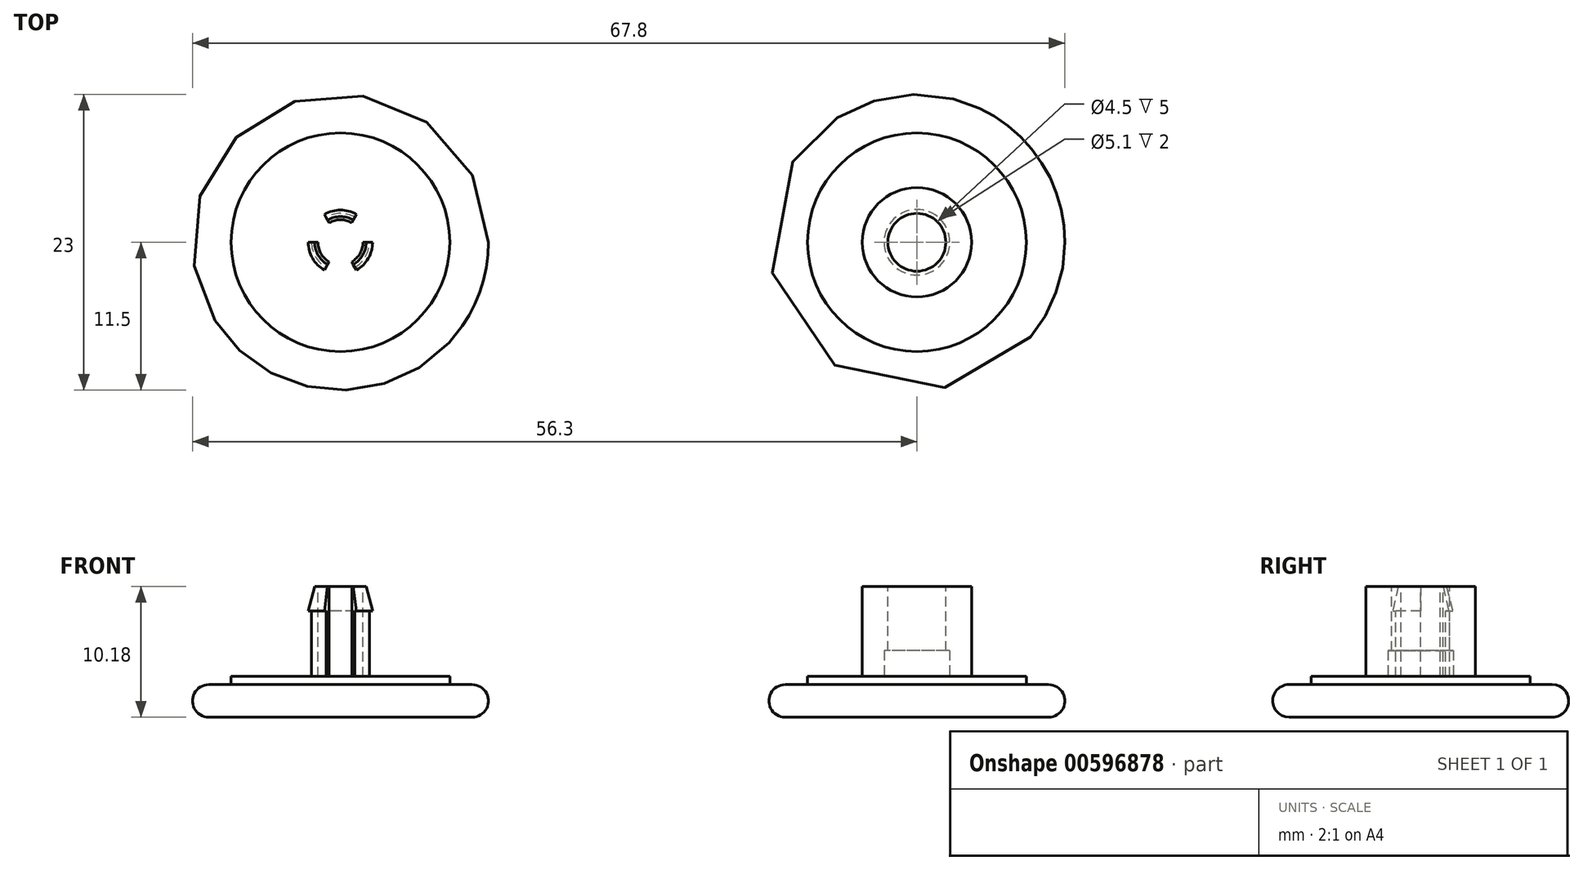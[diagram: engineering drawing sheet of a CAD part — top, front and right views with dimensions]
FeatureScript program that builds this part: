
annotation { "Feature Type Name" : "Feature", "Feature Type Description" : "" }
export const myFeature = defineFeature(function(context is Context, id is Id, definition is map)
    precondition{}
    {
        {
            var Q0;
            Q0=qCreatedBy(makeId("Top.planeOp"),FACE);
            var sketch = newSketch(context, id + "F0", { "sketchPlane" : qUnion([Q0])});
            skCircle(sketch, "E0", {"center": v(0, 0) * mm, "radius": 11.5 * mm});
            skCircle(sketch, "E1", {"center": v(0, 0) * mm, "radius": 4.25 * mm});
            skCircle(sketch, "E2", {"center": v(0, 0) * mm, "radius": 8.5 * mm});
            skSolve(sketch);
        }
        {
            var Q0;
            Q0=makeQuery(id+"F0.imprint","IMPRINT",FACE,{"disambiguationData":[TD([[makeQuery(id+"F0.imprint","IMPRINT",EDGE,{"derivedFrom":sQuery(id+"F0.wireOp",EDGE,"E0")}),1.0]])]});
            extrude(context, id + "F1", {"entities" : qUnion([Q0]), "depth" : 2.54 * mm});
        }
        {
            var Q0;
            Q0=makeQuery(id+"F0.imprint","IMPRINT",FACE,{"disambiguationData":[TD([[makeQuery(id+"F0.imprint","IMPRINT",EDGE,{"derivedFrom":sQuery(id+"F0.wireOp",EDGE,"E1")}),-1.0]])]});
            extrude(context, id + "F2", {"entities" : qUnion([Q0]), "operationType" : NewBodyOperationType.ADD, "depth" : 3.17 * mm});
        }
        {
            var Q0;
            Q0=makeQuery(id+"F0.imprint","IMPRINT",FACE,{"disambiguationData":[TD([[makeQuery(id+"F0.imprint","IMPRINT",EDGE,{"derivedFrom":sQuery(id+"F0.wireOp",EDGE,"E1")}),1.0]])]});
            extrude(context, id + "F3", {"entities" : qUnion([Q0]), "operationType" : NewBodyOperationType.ADD, "depth" : 7 * mm + 3.17 * mm});
        }
        {
            var Q0;
            Q0=makeQuery(id+"F1.opExtrude","CAP_EDGE",EDGE,{"disambiguationData":[OSD([sQuery(id+"F0.wireOp",EDGE,"E0")])],"isStart":false});
            var Q1;
            Q1=makeQuery(id+"F1.opExtrude","CAP_EDGE",EDGE,{"disambiguationData":[OSD([sQuery(id+"F0.wireOp",EDGE,"E0")])],"isStart":true});
            fillet(context, id + "F4", {"entities" : qUnion([Q0, Q1]), "radius" : 1.27 * mm, "tangentPropagation" : true, "allowEdgeOverflow" : false});
        }
        {
            var Q0;
            Q0=qCreatedBy(makeId("Top.planeOp"),FACE);
            var sketch = newSketch(context, id + "F5", { "sketchPlane" : qUnion([Q0])});
            skCircle(sketch, "E3", {"center": v(-44.8, 0) * mm, "radius": 11.5 * mm});
            skCircle(sketch, "E4", {"center": v(-44.8, 0) * mm, "radius": 8.5 * mm});
            skCircle(sketch, "E5", {"center": v(-44.8, 0) * mm, "radius": 2.5 * mm});
            skSolve(sketch);
        }
        {
            var Q0;
            Q0=makeQuery(id+"F5.imprint","IMPRINT",FACE,{"disambiguationData":[TD([[makeQuery(id+"F5.imprint","IMPRINT",EDGE,{"derivedFrom":sQuery(id+"F5.wireOp",EDGE,"E3")}),1.0]])]});
            extrude(context, id + "F6", {"entities" : qUnion([Q0]), "depth" : 2.54 * mm});
        }
        {
            var Q0;
            Q0=makeQuery(id+"F5.imprint","IMPRINT",FACE,{"disambiguationData":[TD([[makeQuery(id+"F5.imprint","IMPRINT",EDGE,{"derivedFrom":sQuery(id+"F5.wireOp",EDGE,"E4")}),1.0]])]});
            extrude(context, id + "F7", {"entities" : qUnion([Q0]), "operationType" : NewBodyOperationType.ADD, "depth" : 3.17 * mm});
        }
        {
            var Q0;
            Q0=makeQuery(id+"F5.imprint","IMPRINT",FACE,{"disambiguationData":[TD([[makeQuery(id+"F5.imprint","IMPRINT",EDGE,{"derivedFrom":sQuery(id+"F5.wireOp",EDGE,"E5")}),1.0]])]});
            extrude(context, id + "F8", {"entities" : qUnion([Q0]), "operationType" : NewBodyOperationType.ADD, "depth" : 7 * mm + 3.17 * mm});
        }
        {
            var Q0;
            Q0=makeQuery(id+"F3.opExtrude","CAP_FACE",FACE,{"disambiguationData":[OSD([sQuery(id+"F0.wireOp",EDGE,"E1")])],"isStart":false});
            var sketch = newSketch(context, id + "F9", { "sketchPlane" : qUnion([Q0])});
            skCircle(sketch, "E6", {"center": v(0, 0) * mm, "radius": 2.25 * mm});
            skSolve(sketch);
        }
        {
            var Q0;
            Q0=makeQuery(id+"F9.imprint","IMPRINT",FACE,{"disambiguationData":[TD([[makeQuery(id+"F9.imprint","IMPRINT",EDGE,{"derivedFrom":sQuery(id+"F9.wireOp",EDGE,"E6")}),1.0]])]});
            extrude(context, id + "F10", {"entities" : qUnion([Q0]), "operationType" : NewBodyOperationType.REMOVE, "oppositeDirection" : true, "depth" : 7 * mm});
        }
        {
            var Q0;
            Q0=makeQuery(id+"F6.opExtrude","CAP_EDGE",EDGE,{"disambiguationData":[OSD([sQuery(id+"F5.wireOp",EDGE,"E3")])],"isStart":false});
            var Q1;
            Q1=makeQuery(id+"F6.opExtrude","CAP_EDGE",EDGE,{"disambiguationData":[OSD([sQuery(id+"F5.wireOp",EDGE,"E3")])],"isStart":true});
            fillet(context, id + "F11", {"entities" : qUnion([Q0, Q1]), "radius" : 1.27 * mm, "tangentPropagation" : true, "allowEdgeOverflow" : false});
        }
        {
            var Q0;
            Q0=makeQuery(id+"F2.opExtrude","CAP_FACE",FACE,{"disambiguationData":[OSD([sQuery(id+"F0.wireOp",EDGE,"E1"),sQuery(id+"F0.wireOp",EDGE,"E2")])],"isStart":false});
            var sketch = newSketch(context, id + "F12", { "sketchPlane" : qUnion([Q0])});
            skCircle(sketch, "E7", {"center": v(0, 0) * mm, "radius": 2.55 * mm});
            skSolve(sketch);
        }
        {
            var Q0;
            Q0 = qSketchRegion(id + "F12", true);
            extrude(context, id + "F13", {"entities" : qUnion([Q0]), "operationType" : NewBodyOperationType.REMOVE, "depth" : 2 * mm, "offsetDistance" : 25.4 * mm});
        }
        {
            var Q0;
            Q0=qCreatedBy(makeId("Front.planeOp"),FACE);
            var sketch = newSketch(context, id + "F14", { "sketchPlane" : qUnion([Q0])});
            skLineSegment(sketch, "E8", {"start": v(-44.8, 0) * mm, "end": v(-44.8, 10.18) * mm});
            skLineSegment(sketch, "E9", {"start": v(-44.8, 10.18) * mm, "end": v(-42.55, 10.18) * mm});
            skLineSegment(sketch, "E10", {"start": v(-42.55, 8.27) * mm, "end": v(-42.3, 8.27) * mm});
            skLineSegment(sketch, "E11", {"start": v(-42.55, 8.27) * mm, "end": v(-42.55, 3.17) * mm});
            skLineSegment(sketch, "E12", {"start": v(-42.55, 10.18) * mm, "end": v(-41.88, 10.26) * mm});
            skLineSegment(sketch, "E13", {"start": v(-42.55, 3.17) * mm, "end": v(-41.9, 3.17) * mm});
            skLineSegment(sketch, "E14", {"start": v(-42.3, 8.27) * mm, "end": v(-41.64, 8.27) * mm});
            skLineSegment(sketch, "E15", {"start": v(-41.64, 8.27) * mm, "end": v(-41.88, 10.26) * mm});
            skLineSegment(sketch, "E16", {"start": v(-41.9, 3.17) * mm, "end": v(-41.64, 8.27) * mm});
            skPoint(sketch, "E17", {"position": v(-42.8, 10.18) * mm});
            skLineSegment(sketch, "E18", {"start": v(-42.3, 8.27) * mm, "end": v(-42.8, 10.18) * mm});
            skLineSegment(sketch, "E19", {"start": v(-42.55, 3.17) * mm, "end": v(-44.8, 3.17) * mm});
            skLineSegment(sketch, "E20", {"start": v(-42.8, 10.18) * mm, "end": v(-42.8, 3.17) * mm});
            skLineSegment(sketch, "E21", {"start": v(-43.3, 10.18) * mm, "end": v(-43.3, 3.17) * mm});
            skSolve(sketch);
        }
        {
            var Q0;
            Q0=makeQuery(id+"F14.imprint","IMPRINT",FACE,{"disambiguationData":[TD([[makeQuery(id+"F14.imprint","IMPRINT",EDGE,{"derivedFrom":sQuery(id+"F14.wireOp",EDGE,"E10")}),-1.0]])]});
            var Q1;
            {var subQ0=sQuery(id+"F14.wireOp",EDGE,"E12");Q1=makeQuery(id+"F14.imprint","IMPRINT",FACE,{"disambiguationData":[TD([[makeQuery(id+"F14.imprint","IMPRINT",EDGE,{"derivedFrom":subQ0}),-1.0]])]});}
            var Q2;
            Q2=sQuery(id+"F14.wireOp",EDGE,"E8");
            revolve(context, id + "F15", {"operationType" : NewBodyOperationType.REMOVE, "entities" : qUnion([Q0, Q1]), "axis" : qUnion([Q2]), "revolveType" : RevolveType.FULL, "oppositeDirection" : true});
        }
        {
            var Q0;
            Q0=makeQuery(id+"F8.opExtrude","CAP_FACE",FACE,{"disambiguationData":[OSD([sQuery(id+"F5.wireOp",EDGE,"E5")])],"isStart":false});
            var sketch = newSketch(context, id + "F16", { "sketchPlane" : qUnion([Q0])});
            skCircle(sketch, "E22", {"center": v(-44.8, 0) * mm, "radius": 1.75 * mm});
            skSolve(sketch);
        }
        {
            var Q0;
            Q0 = qSketchRegion(id + "F16", true);
            extrude(context, id + "F17", {"entities" : qUnion([Q0]), "operationType" : NewBodyOperationType.REMOVE, "oppositeDirection" : true, "depth" : 7 * mm, "offsetDistance" : 25.4 * mm});
        }
        {
            var Q0;
            Q0=makeQuery(id+"F15.boolean.opBoolean","MERGE",FACE,{"derivedFrom":[makeQuery(id+"F7.opExtrude","CAP_FACE",FACE,{"disambiguationData":[OSD([sQuery(id+"F5.wireOp",EDGE,"E4"),sQuery(id+"F5.wireOp",EDGE,"E5")])],"isStart":false}),makeQuery(id+"F15.opRevolve","SWEPT_FACE",FACE,{"disambiguationData":[OSD([sQuery(id+"F14.wireOp",EDGE,"E13")])]})]});
            var sketch = newSketch(context, id + "F18", { "sketchPlane" : qUnion([Q0])});
            skCircle(sketch, "E23", {"center": v(-44.8, 0) * mm, "radius": 4.95 * mm});
            skLineSegment(sketch, "E24", {"start": v(-44.8, 0) * mm, "end": v(-44.8, 4.95) * mm});
            skLineSegment(sketch, "E25", {"start": v(-44.8, 0) * mm, "end": v(-40.51, -2.47) * mm});
            skLineSegment(sketch, "E26", {"start": v(-44.8, 0) * mm, "end": v(-49.08, -2.47) * mm});
            skLineSegment(sketch, "E27", {"start": v(-44.8, 0) * mm, "end": v(-42.32, 4.28) * mm});
            skLineSegment(sketch, "E28", {"start": v(-44.8, 0) * mm, "end": v(-39.85, 0) * mm});
            skLineSegment(sketch, "E29", {"start": v(-44.8, 0) * mm, "end": v(-47.27, 4.28) * mm});
            skLineSegment(sketch, "E30", {"start": v(-44.8, 0) * mm, "end": v(-49.75, 0) * mm});
            skLineSegment(sketch, "E31", {"start": v(-44.8, 0) * mm, "end": v(-47.27, -4.28) * mm});
            skLineSegment(sketch, "E32", {"start": v(-44.8, 0) * mm, "end": v(-42.32, -4.28) * mm});
            skSolve(sketch);
        }
        {
            var Q0;
            {var subQ0=sQuery(id+"F18.wireOp",EDGE,"E29");var subQ1=sQuery(id+"F18.wireOp",EDGE,"E23");var subQ2=makeQuery(id+"F18.imprint","INTERSECT",VERTEX,{"derivedFrom":[subQ1,subQ0]});Q0=makeQuery(id+"F18.imprint","IMPRINT",FACE,{"disambiguationData":[TD([[makeQuery(id+"F18.imprint","IMPRINT",EDGE,{"disambiguationData":[TD([[subQ2,-1.0]])],"derivedFrom":subQ1}),1.0]])]});}
            var Q1;
            {var subQ1=sQuery(id+"F18.wireOp",EDGE,"E29");var subQ3=makeQuery(id+"F15.boolean.opBoolean","COPY",EDGE,{"derivedFrom":makeQuery(id+"F15.opRevolve","SWEPT_EDGE",EDGE,{"disambiguationData":[OSD([sQuery(id+"F14.wireOp",EDGE,"E11"),sQuery(id+"F14.wireOp",EDGE,"E13"),sQuery(id+"F14.wireOp",EDGE,"E19")])]})});var subQ4=makeQuery(id+"F18.imprint","INTERSECT",VERTEX,{"derivedFrom":[subQ3,subQ1]});Q1=makeQuery(id+"F18.imprint","IMPRINT",FACE,{"disambiguationData":[TD([[makeQuery(id+"F18.imprint","IMPRINT",EDGE,{"disambiguationData":[TD([[subQ4,-1.0]])],"derivedFrom":subQ3}),1.0]])]});}
            var Q2;
            {var subQ0=sQuery(id+"F18.wireOp",EDGE,"E27");var subQ1=sQuery(id+"F18.wireOp",EDGE,"E23");var subQ2=makeQuery(id+"F18.imprint","INTERSECT",VERTEX,{"derivedFrom":[subQ1,subQ0]});Q2=makeQuery(id+"F18.imprint","IMPRINT",FACE,{"disambiguationData":[TD([[makeQuery(id+"F18.imprint","IMPRINT",EDGE,{"disambiguationData":[TD([[subQ2,1.0]])],"derivedFrom":subQ1}),1.0]])]});}
            var Q3;
            {var subQ1=sQuery(id+"F18.wireOp",EDGE,"E27");var subQ3=makeQuery(id+"F15.boolean.opBoolean","COPY",EDGE,{"derivedFrom":makeQuery(id+"F15.opRevolve","SWEPT_EDGE",EDGE,{"disambiguationData":[OSD([sQuery(id+"F14.wireOp",EDGE,"E11"),sQuery(id+"F14.wireOp",EDGE,"E13"),sQuery(id+"F14.wireOp",EDGE,"E19")])]})});var subQ4=makeQuery(id+"F18.imprint","INTERSECT",VERTEX,{"derivedFrom":[subQ3,subQ1]});Q3=makeQuery(id+"F18.imprint","IMPRINT",FACE,{"disambiguationData":[TD([[makeQuery(id+"F18.imprint","IMPRINT",EDGE,{"disambiguationData":[TD([[subQ4,1.0]])],"derivedFrom":subQ3}),1.0]])]});}
            var Q4;
            {var subQ0=sQuery(id+"F18.wireOp",EDGE,"E31");var subQ1=sQuery(id+"F18.wireOp",EDGE,"E23");var subQ2=makeQuery(id+"F18.imprint","INTERSECT",VERTEX,{"derivedFrom":[subQ1,subQ0]});Q4=makeQuery(id+"F18.imprint","IMPRINT",FACE,{"disambiguationData":[TD([[makeQuery(id+"F18.imprint","IMPRINT",EDGE,{"disambiguationData":[TD([[subQ2,-1.0]])],"derivedFrom":subQ1}),1.0]])]});}
            var Q5;
            {var subQ1=sQuery(id+"F18.wireOp",EDGE,"E31");var subQ3=makeQuery(id+"F15.boolean.opBoolean","COPY",EDGE,{"derivedFrom":makeQuery(id+"F15.opRevolve","SWEPT_EDGE",EDGE,{"disambiguationData":[OSD([sQuery(id+"F14.wireOp",EDGE,"E11"),sQuery(id+"F14.wireOp",EDGE,"E13"),sQuery(id+"F14.wireOp",EDGE,"E19")])]})});var subQ4=makeQuery(id+"F18.imprint","INTERSECT",VERTEX,{"derivedFrom":[subQ3,subQ1]});Q5=makeQuery(id+"F18.imprint","IMPRINT",FACE,{"disambiguationData":[TD([[makeQuery(id+"F18.imprint","IMPRINT",EDGE,{"disambiguationData":[TD([[subQ4,-1.0]])],"derivedFrom":subQ3}),1.0]])]});}
            extrude(context, id + "F19", {"entities" : qUnion([Q0, Q1, Q2, Q3, Q4, Q5]), "operationType" : NewBodyOperationType.REMOVE, "depth" : 25.4 * mm, "offsetDistance" : 25.4 * mm});
        }
    });
